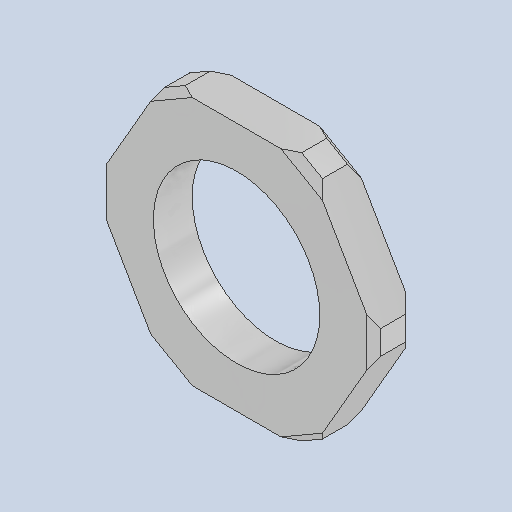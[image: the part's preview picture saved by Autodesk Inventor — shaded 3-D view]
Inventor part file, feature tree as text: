
AUTODESK INVENTOR PART (.ipt)
format: ipt  version: 2024.2 (Build 282272000, 272)  size: 136,704 bytes
history: native  units: mm
features: extrude x2, chamfer x2, sketch x1
ambient origin geometry x8: Origin, YZ Plane, XZ Plane, XY Plane, X Axis, Y Axis, Z Axis, Center Point
bodies: Solid1 (feature_tree)
feature tree (5):
  extrude  "Extrusion1"  Depth=2.8mm TaperAngle=0.0deg
  extrude  "Extrusion2"  Depth=2.8mm
  chamfer  "Chamfer1"  Distance=2.8mm
  chamfer  "Chamfer2"  Distance=1.0mm Angle=45.0deg
  sketch  "Sketch1"  dims[d0=18.0mm d1=2.8mm d2=0.0mm d3=12.0mm d4=2.8mm d5=0.0mm d6=1.0mm d7=2.0mm d8=45.0deg d9=0.5mm d10=2.0mm d11=45.0deg]
